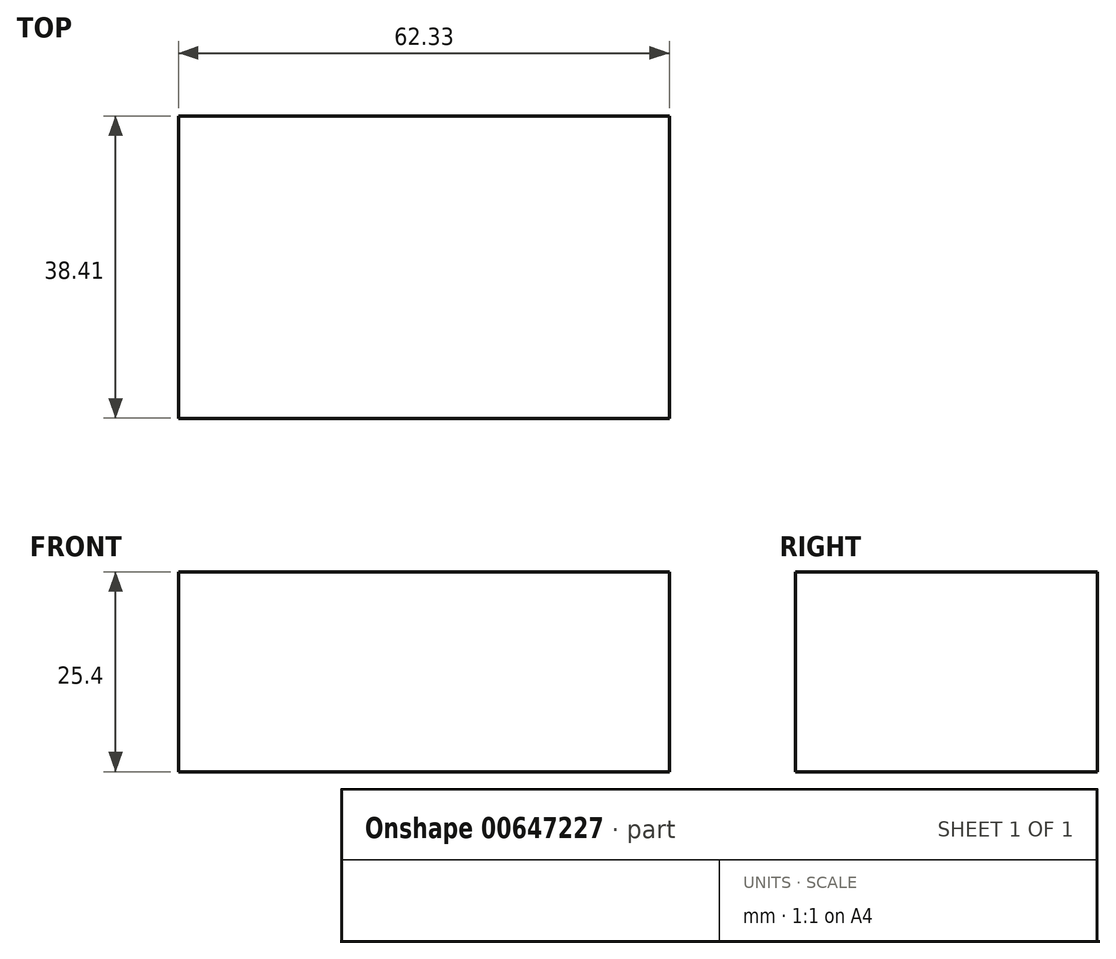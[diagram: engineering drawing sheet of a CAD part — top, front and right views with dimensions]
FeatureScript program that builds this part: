
annotation { "Feature Type Name" : "Feature", "Feature Type Description" : "" }
export const myFeature = defineFeature(function(context is Context, id is Id, definition is map)
    precondition{}
    {
        {
            var Q0;
            Q0=qCreatedBy(makeId("Top.planeOp"),FACE);
            var sketch = newSketch(context, id + "F0", { "sketchPlane" : qUnion([Q0])});
            skLineSegment(sketch, "E0.bottom", {"start": v(0, 0) * mm, "end": v(62.33, 0) * mm});
            skLineSegment(sketch, "E0.top", {"start": v(0, -38.41) * mm, "end": v(62.33, -38.41) * mm});
            skLineSegment(sketch, "E0.left", {"start": v(0, 0) * mm, "end": v(0, -38.41) * mm});
            skLineSegment(sketch, "E0.right", {"start": v(62.33, 0) * mm, "end": v(62.33, -38.41) * mm});
            skSolve(sketch);
        }
        {
            var Q0;
            Q0 = qSketchRegion(id + "F0", true);
            extrude(context, id + "F1", {"entities" : qUnion([Q0]), "depth" : 25.4 * mm, "offsetDistance" : 25.4 * mm});
        }
    });
